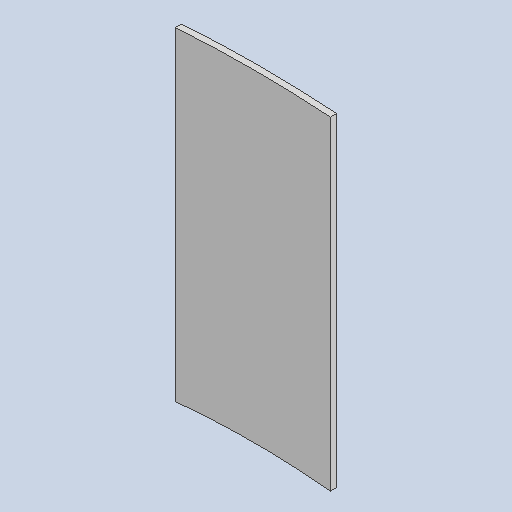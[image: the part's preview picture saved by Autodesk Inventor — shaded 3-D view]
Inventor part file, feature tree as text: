
AUTODESK INVENTOR PART (.ipt)
format: ipt  version: 2025 (Build 290162010, 162A)  size: 149,504 bytes
history: native  units: mm
features: sheet_metal_op x1, sketch x1, other x1
ambient origin geometry x8: Origin, YZ Plane, XZ Plane, XY Plane, X Axis, Y Axis, Z Axis, Center Point
bodies: Solid1 (feature_tree)
feature tree (3):
  sheet_metal_op  "Face1"
  sketch  "Sketch1"  dims[d15=2.0mm d26=512.0mm d27=50.0mm d28=720.0mm]
  other  "Plate1"
